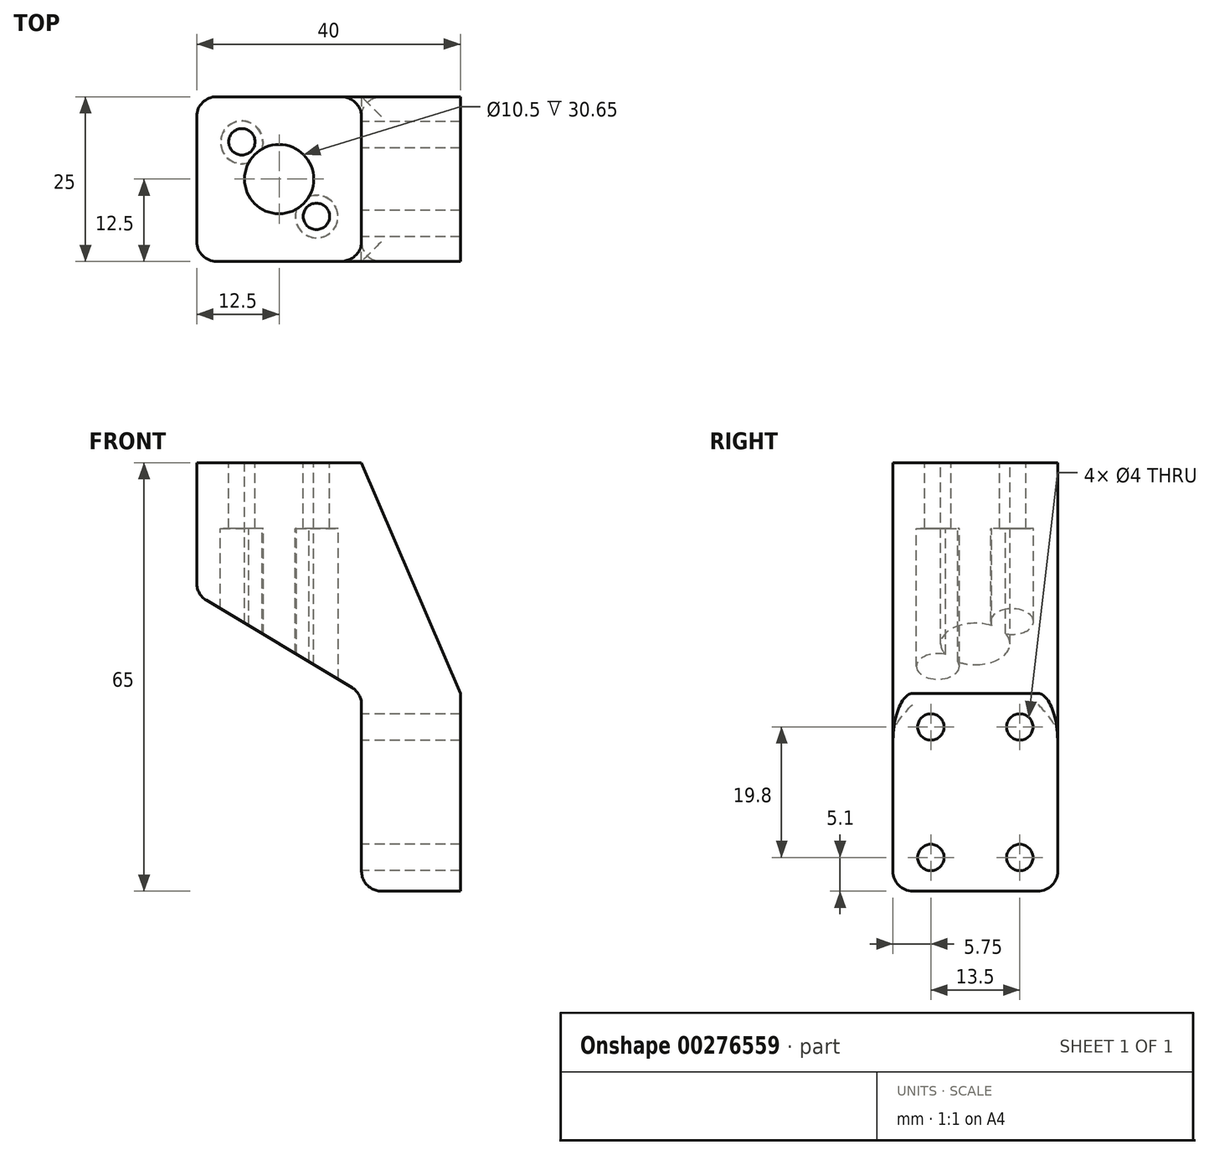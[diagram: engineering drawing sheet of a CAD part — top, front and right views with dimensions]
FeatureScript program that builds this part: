
annotation { "Feature Type Name" : "Feature", "Feature Type Description" : "" }
export const myFeature = defineFeature(function(context is Context, id is Id, definition is map)
    precondition{}
    {
        {
            var Q0;
            Q0=qCreatedBy(makeId("Front.planeOp"),FACE);
            var sketch = newSketch(context, id + "F0", { "sketchPlane" : qUnion([Q0])});
            skLineSegment(sketch, "E0.bottom", {"start": v(12.5, -10) * mm, "end": v(-12.5, -10) * mm});
            skLineSegment(sketch, "E0.top", {"start": v(12.5, 10) * mm, "end": v(-12.5, 10) * mm});
            skLineSegment(sketch, "E0.left", {"start": v(12.5, -10) * mm, "end": v(12.5, 10) * mm});
            skLineSegment(sketch, "E0.right", {"start": v(-12.5, -10) * mm, "end": v(-12.5, 10) * mm});
            skPoint(sketch, "E0.middle", {"position": v(0, 0) * mm});
            skLineSegment(sketch, "E1.bottom", {"start": v(12.5, -25) * mm, "end": v(27.5, -25) * mm});
            skLineSegment(sketch, "E1.top", {"start": v(12.5, -55) * mm, "end": v(27.5, -55) * mm});
            skLineSegment(sketch, "E1.left", {"start": v(12.5, -25) * mm, "end": v(12.5, -55) * mm});
            skLineSegment(sketch, "E1.right", {"start": v(27.5, -25) * mm, "end": v(27.5, -55) * mm});
            skLineSegment(sketch, "E2", {"start": v(12.5, 10) * mm, "end": v(27.5, -25) * mm});
            skLineSegment(sketch, "E3", {"start": v(-12.5, -10) * mm, "end": v(12.5, -25) * mm});
            skSolve(sketch);
        }
        {
            var Q0;
            Q0 = qSketchRegion(id + "F0", true);
            extrude(context, id + "F1", {"entities" : qUnion([Q0]), "depth" : 25 * mm, "offsetDistance" : 25 * mm});
        }
        {
            var Q0;
            Q0=makeQuery(id+"F1.opExtrude","SWEPT_FACE",FACE,{"disambiguationData":[OSD([sQuery(id+"F0.wireOp",EDGE,"E0.top")])]});
            var sketch = newSketch(context, id + "F2", { "sketchPlane" : qUnion([Q0])});
            skLineSegment(sketch, "E4", {"start": v(-12.5, 0) * mm, "end": v(12.5, -25) * mm, "construction": true});
            skCircle(sketch, "E5", {"center": v(0, -12.5) * mm, "radius": 5.25 * mm});
            skSolve(sketch);
        }
        {
            var Q0;
            Q0 = qSketchRegion(id + "F2", true);
            extrude(context, id + "F3", {"entities" : qUnion([Q0]), "operationType" : NewBodyOperationType.REMOVE, "endBound" : BoundingType.THROUGH_ALL, "oppositeDirection" : true, "depth" : 12 * mm, "offsetDistance" : 25 * mm});
        }
        {
            var Q0;
            Q0=makeQuery(id+"F1.opExtrude","SWEPT_FACE",FACE,{"disambiguationData":[OSD([sQuery(id+"F0.wireOp",EDGE,"E1.left")])]});
            var sketch = newSketch(context, id + "F4", { "sketchPlane" : qUnion([Q0])});
            skPoint(sketch, "E6.middle", {"position": v(12.5, -40) * mm});
            skCircle(sketch, "E7", {"center": v(19.25, -30.1) * mm, "radius": 2 * mm});
            skCircle(sketch, "E8", {"center": v(5.75, -49.9) * mm, "radius": 2 * mm});
            skLineSegment(sketch, "E9", {"start": v(12.5, -40) * mm, "end": v(12.5, 51.24) * mm, "construction": true});
            skCircle(sketch, "E10.MirrorC", {"center": v(5.75, -30.1) * mm, "radius": 2 * mm});
            skCircle(sketch, "E11.MirrorC", {"center": v(19.25, -49.9) * mm, "radius": 2 * mm});
            skSolve(sketch);
        }
        {
            var Q0;
            Q0 = qSketchRegion(id + "F4", true);
            extrude(context, id + "F5", {"entities" : qUnion([Q0]), "operationType" : NewBodyOperationType.REMOVE, "oppositeDirection" : true, "depth" : 25 * mm, "offsetDistance" : 25 * mm});
        }
        {
            var Q0;
            Q0=makeQuery(id+"F1.opExtrude","CAP_EDGE",EDGE,{"disambiguationData":[OSD([sQuery(id+"F0.wireOp",EDGE,"E0.right")])],"isStart":false});
            var Q1;
            Q1=makeQuery(id+"F1.opExtrude","CAP_EDGE",EDGE,{"disambiguationData":[OSD([sQuery(id+"F0.wireOp",EDGE,"E0.right")])],"isStart":true});
            var Q2;
            Q2=makeQuery(id+"F1.opExtrude","SWEPT_EDGE",EDGE,{"disambiguationData":[OSD([sQuery(id+"F0.wireOp",EDGE,"E0.bottom"),sQuery(id+"F0.wireOp",EDGE,"E0.right"),sQuery(id+"F0.wireOp",EDGE,"E3")])]});
            var Q3;
            Q3=makeQuery(id+"F1.opExtrude","CAP_EDGE",EDGE,{"disambiguationData":[OSD([sQuery(id+"F0.wireOp",EDGE,"E3")])],"isStart":false});
            var Q4;
            Q4=makeQuery(id+"F1.opExtrude","CAP_EDGE",EDGE,{"disambiguationData":[OSD([sQuery(id+"F0.wireOp",EDGE,"E3")])],"isStart":true});
            var Q5;
            Q5=makeQuery(id+"F1.opExtrude","SWEPT_EDGE",EDGE,{"disambiguationData":[OSD([sQuery(id+"F0.wireOp",EDGE,"E1.bottom"),sQuery(id+"F0.wireOp",EDGE,"E1.left"),sQuery(id+"F0.wireOp",EDGE,"E3")])]});
            var Q6;
            Q6=makeQuery(id+"F1.opExtrude","SWEPT_EDGE",EDGE,{"disambiguationData":[OSD([sQuery(id+"F0.wireOp",EDGE,"E1.top"),sQuery(id+"F0.wireOp",EDGE,"E1.left")])]});
            var Q7;
            Q7=makeQuery(id+"F1.opExtrude","CAP_EDGE",EDGE,{"disambiguationData":[OSD([sQuery(id+"F0.wireOp",EDGE,"E2")])],"isStart":false});
            var Q8;
            Q8=makeQuery(id+"F1.opExtrude","CAP_EDGE",EDGE,{"disambiguationData":[OSD([sQuery(id+"F0.wireOp",EDGE,"E2")])],"isStart":true});
            var Q9;
            Q9=makeQuery(id+"F1.opExtrude","CAP_EDGE",EDGE,{"disambiguationData":[OSD([sQuery(id+"F0.wireOp",EDGE,"E1.top")])],"isStart":false});
            var Q10;
            Q10=makeQuery(id+"F1.opExtrude","CAP_EDGE",EDGE,{"disambiguationData":[OSD([sQuery(id+"F0.wireOp",EDGE,"E1.top")])],"isStart":true});
            fillet(context, id + "F6", {"entities" : qUnion([Q0, Q1, Q2, Q3, Q4, Q5, Q6, Q7, Q8, Q9, Q10]), "tangentPropagation" : true, "radius" : 3 * mm, "defaultsChanged" : false, "vertexSettings" : [], "allowEdgeOverflow" : false});
        }
        {
            var Q0;
            Q0=makeQuery(id+"F1.opExtrude","SWEPT_FACE",FACE,{"disambiguationData":[OSD([sQuery(id+"F0.wireOp",EDGE,"E0.top")])]});
            var sketch = newSketch(context, id + "F7", { "sketchPlane" : qUnion([Q0])});
            skPoint(sketch, "E12.middle", {"position": v(0, -12.5) * mm});
            skCircle(sketch, "E13", {"center": v(-5.66, -6.84) * mm, "radius": 2 * mm});
            skCircle(sketch, "E14", {"center": v(5.66, -18.16) * mm, "radius": 2 * mm});
            skSolve(sketch);
        }
        {
            var Q0;
            Q0 = qSketchRegion(id + "F7", true);
            extrude(context, id + "F8", {"entities" : qUnion([Q0]), "operationType" : NewBodyOperationType.REMOVE, "endBound" : BoundingType.THROUGH_ALL, "oppositeDirection" : true, "depth" : 25 * mm, "offsetDistance" : 25 * mm});
        }
        {
            var Q0;
            Q0=qCreatedBy(makeId("Top.planeOp"),FACE);
            var sketch = newSketch(context, id + "F9", { "sketchPlane" : qUnion([Q0])});
            skCircle(sketch, "E15", {"center": v(-5.66, -6.92) * mm, "radius": 3.25 * mm});
            skCircle(sketch, "E16", {"center": v(5.7, -18.18) * mm, "radius": 3.25 * mm});
            skSolve(sketch);
        }
        {
            var Q0;
            Q0 = qSketchRegion(id + "F9", true);
            extrude(context, id + "F10", {"entities" : qUnion([Q0]), "operationType" : NewBodyOperationType.REMOVE, "endBound" : BoundingType.THROUGH_ALL, "oppositeDirection" : true, "depth" : 25 * mm, "offsetDistance" : 25 * mm});
        }
    });
